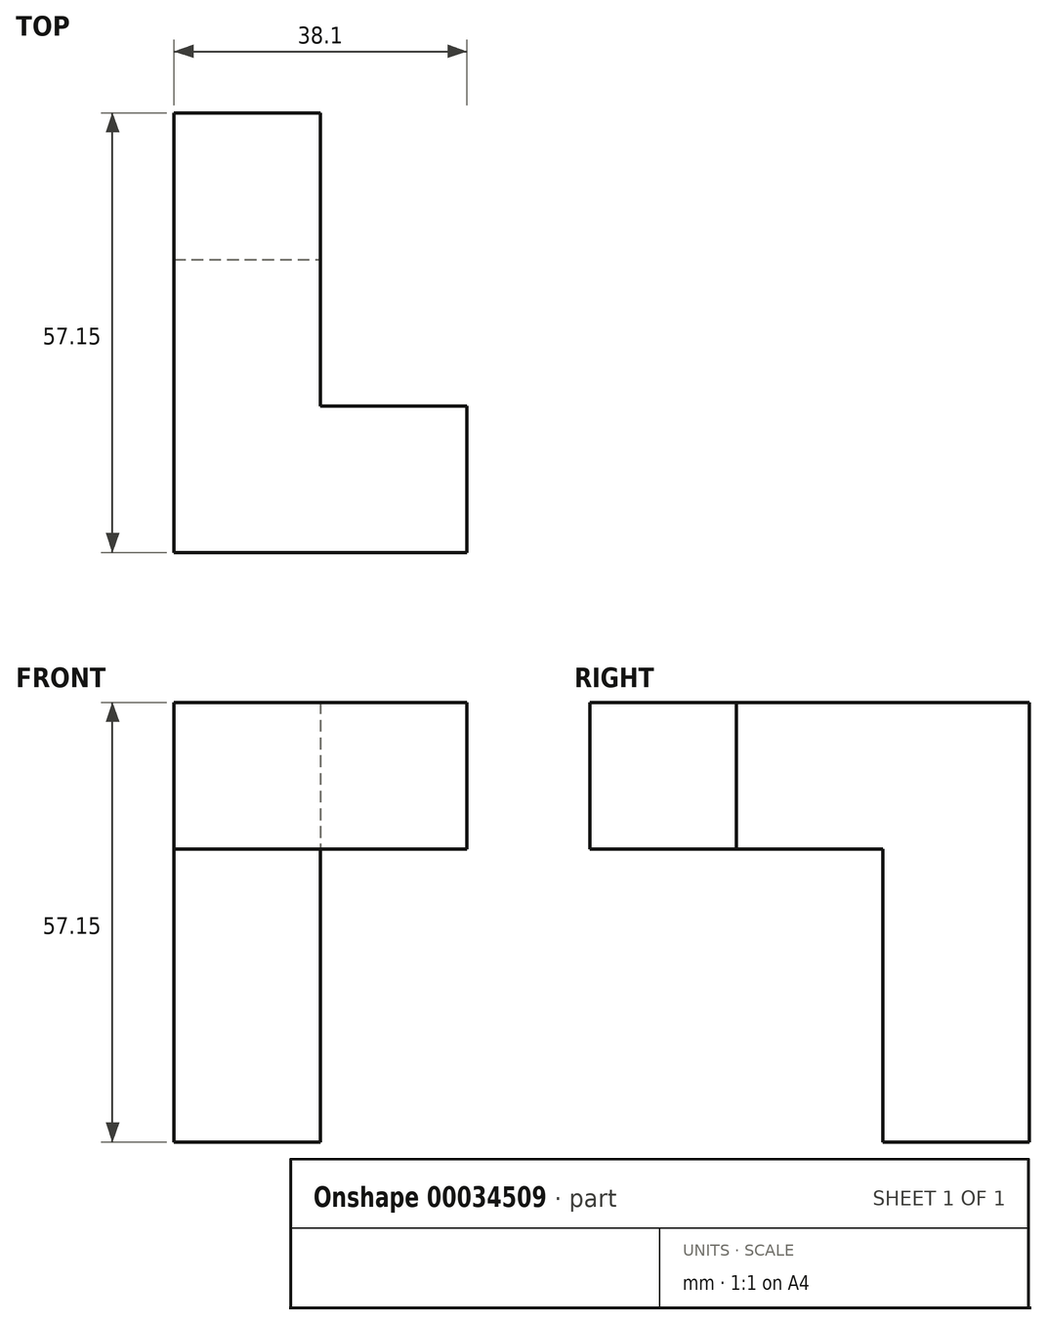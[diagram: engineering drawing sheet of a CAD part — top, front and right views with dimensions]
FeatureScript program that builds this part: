
annotation { "Feature Type Name" : "Feature", "Feature Type Description" : "" }
export const myFeature = defineFeature(function(context is Context, id is Id, definition is map)
    precondition{}
    {
        {
            var Q0;
            Q0=qCreatedBy(makeId("Front.planeOp"),FACE);
            var sketch = newSketch(context, id + "F0", { "sketchPlane" : qUnion([Q0])});
            skLineSegment(sketch, "E0.bottom", {"start": v(0, 0) * mm, "end": v(19.05, 0) * mm});
            skLineSegment(sketch, "E0.top", {"start": v(0, 57.15) * mm, "end": v(19.05, 57.15) * mm});
            skLineSegment(sketch, "E0.left", {"start": v(0, 0) * mm, "end": v(0, 57.15) * mm});
            skLineSegment(sketch, "E0.right", {"start": v(19.05, 0) * mm, "end": v(19.05, 57.15) * mm});
            skSolve(sketch);
        }
        {
            var Q0;
            Q0 = qSketchRegion(id + "F0", true);
            extrude(context, id + "F1", {"entities" : qUnion([Q0]), "depth" : 19.05 * mm});
        }
        {
            var Q0;
            Q0=makeQuery(id+"F1.opExtrude","CAP_FACE",FACE,{"disambiguationData":[OSD([sQuery(id+"F0.wireOp",EDGE,"E0.bottom"),sQuery(id+"F0.wireOp",EDGE,"E0.top"),sQuery(id+"F0.wireOp",EDGE,"E0.left"),sQuery(id+"F0.wireOp",EDGE,"E0.right")])],"isStart":false});
            var sketch = newSketch(context, id + "F2", { "sketchPlane" : qUnion([Q0])});
            skLineSegment(sketch, "E1.bottom", {"start": v(0, 57.15) * mm, "end": v(19.05, 57.15) * mm});
            skLineSegment(sketch, "E1.top", {"start": v(0, 38.1) * mm, "end": v(19.05, 38.1) * mm});
            skLineSegment(sketch, "E1.left", {"start": v(0, 57.15) * mm, "end": v(0, 38.1) * mm});
            skLineSegment(sketch, "E1.right", {"start": v(19.05, 57.15) * mm, "end": v(19.05, 38.1) * mm});
            skSolve(sketch);
        }
        {
            var Q0;
            Q0 = qSketchRegion(id + "F2", true);
            extrude(context, id + "F3", {"entities" : qUnion([Q0]), "operationType" : NewBodyOperationType.ADD, "depth" : 38.1 * mm});
        }
        {
            var Q0;
            Q0=makeQuery(id+"F3.boolean.opBoolean","MERGE",FACE,{"derivedFrom":[makeQuery(id+"F1.opExtrude","SWEPT_FACE",FACE,{"disambiguationData":[OSD([sQuery(id+"F0.wireOp",EDGE,"E0.right")])]}),makeQuery(id+"F3.opExtrude","SWEPT_FACE",FACE,{"disambiguationData":[OSD([sQuery(id+"F2.wireOp",EDGE,"E1.right")])]})]});
            var sketch = newSketch(context, id + "F4", { "sketchPlane" : qUnion([Q0])});
            skLineSegment(sketch, "E2.bottom", {"start": v(-57.15, 57.15) * mm, "end": v(-38.1, 57.15) * mm});
            skLineSegment(sketch, "E2.top", {"start": v(-57.15, 38.1) * mm, "end": v(-38.1, 38.1) * mm});
            skLineSegment(sketch, "E2.left", {"start": v(-57.15, 57.15) * mm, "end": v(-57.15, 38.1) * mm});
            skLineSegment(sketch, "E2.right", {"start": v(-38.1, 57.15) * mm, "end": v(-38.1, 38.1) * mm});
            skSolve(sketch);
        }
        {
            var Q0;
            Q0 = qSketchRegion(id + "F4", true);
            extrude(context, id + "F5", {"entities" : qUnion([Q0]), "operationType" : NewBodyOperationType.ADD, "depth" : 19.05 * mm});
        }
    });
